# Revit family: PRD_FrankeWS_PprTwlDspnsrs_RODANPaperTowelDispenser_RODX600ME
name_source: partatom
category: Furniture
revit_build: Autodesk Revit 2018 (Build: 20190510_1515(x64)
units: mm (PartAtom-declared; Revit-internal decimal feet)

## family parameters
Cut with Voids When Loaded = No
Host = Face
OmniClass Number = 23.40.20.21
OmniClass Title = Toilet and Bath Specialties
Room Calculation Point = No
Shared = No

## types (1)
- RODX600ME
    AssetType = Fixed
    BIMObjectName = PRD_AR_PprTwlDspnsrs_RodanPaperTowelDispenser_RODX600ME
    Category = Pr_40_70_22_62, Paper towel dispensers
    Color = no colour
    Default Elevation = 1200 mm
    Description = Paper towel dispenser for hidden mounting behind wall and mirror, stainless steel, surface satin finished, material thickness 0.8 mm, for 600 - 800 paper towels, depending on convolution, filling from bottom, incl. stainless steel screws and dowels
    DispenserMaterial = PRD_AR_StainlessSteel_SatinFinished
    DurationUnit = year
    Features = stainless steel, surface satin finished, material thickness 0.8 mm
    FillingQuantity = 800 towels
    Finish = satin finished
    Form = Wall mounted
    GrossWeight = 4.06 kg
    IfcExportAs = IfcFurnitureType
    IfcExportType = USERDEFINED
    IntegralAccessories = Stainless steel screws and dowels incl.
    Lock = no lock
    MainColor = stainless steel
    Manufacturer = KWC Group AG
    ManufacturerName = KWC Group AG
    ManufacturerURL = www.kwc.com
    Material = stainless steel
    MaterialThickness = 0.80 mm
    MaterialsBody = Stainless steel
    MaterialsFinishAndColour = Stainless steel, satin finished
    MaximumDepthOfConsumable = 85 mm  [stored 0.278871 ft]
    MaximumWidthOfConsumable = 270 mm  [stored 0.885827 ft]
    Model = RODX600ME
    ModelNumber = 2000090058
    ModelReference = RODX600ME
    NBSDescription = Paper towel dispensers
    NBSReference = 45-35-72/344
    Name = Rodan paper towel dispenser RODX600ME
    NetWeight = 3.60 kg
    NominalDepth = 113 mm  [stored 0.370735 ft]
    NominalHeight = 464 mm  [stored 1.52231 ft]
    NominalWidth = 342 mm  [stored 1.12205 ft]
    ProductInformation = https://pim.kwc.com
    Size = 113 x 464 x 342 mm
    Style = paper towel dispenser
    TypeOfConsumable = paper towel
    TypeOfFixing = screw
    TypeOfMounting = various types
    TypeOfOperation = manual operation
    URL = www.kwc.com
    Uniclass2015Code = Pr_40_70_22_62
    Uniclass2015Title = Paper towel dispensers
    Uniclass2015Version = Products v1.10
    Version = 1
    WarrantyDurationUnit = year

note: [stored X ft] marks values corroborated as IEEE doubles in the binary element streams (Revit-internal decimal feet)

## geometry (parser evidence)
native form markers: Sweep x2
no freeform markers — native parametric forms only
